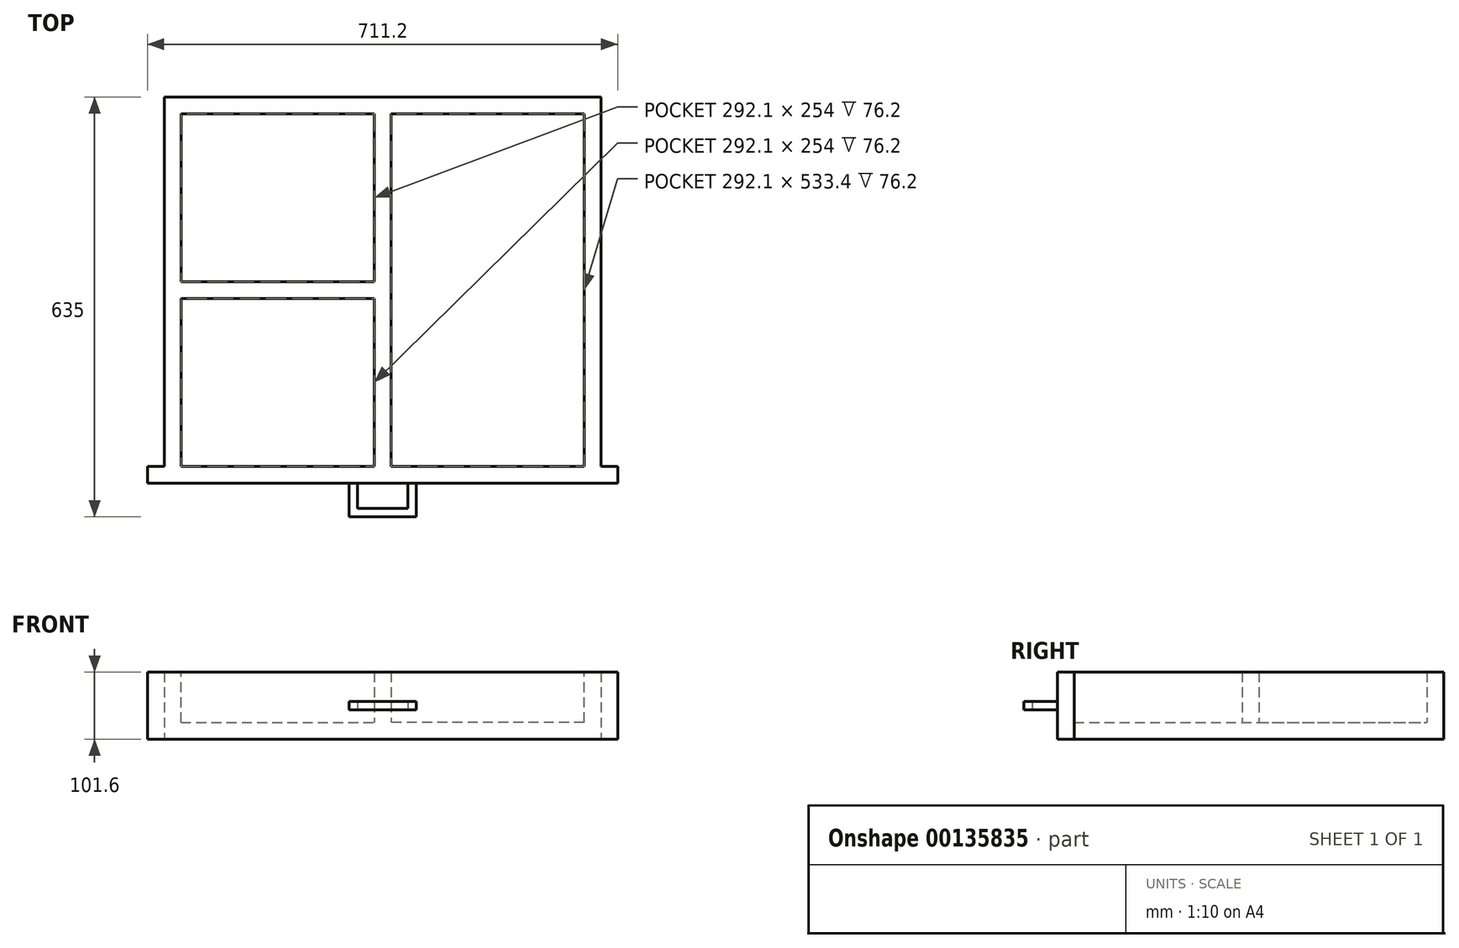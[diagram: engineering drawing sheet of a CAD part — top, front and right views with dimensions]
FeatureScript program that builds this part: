
annotation { "Feature Type Name" : "Feature", "Feature Type Description" : "" }
export const myFeature = defineFeature(function(context is Context, id is Id, definition is map)
    precondition{}
    {
        {
            var Q0;
            Q0=qCreatedBy(makeId("Front.planeOp"),FACE);
            var sketch = newSketch(context, id + "F0", { "sketchPlane" : qUnion([Q0])});
            skLineSegment(sketch, "E0.bottom", {"start": v(-355.6, 50.8) * mm, "end": v(355.6, 50.8) * mm});
            skLineSegment(sketch, "E0.top", {"start": v(-355.6, -50.8) * mm, "end": v(355.6, -50.8) * mm});
            skLineSegment(sketch, "E0.left", {"start": v(-355.6, 50.8) * mm, "end": v(-355.6, -50.8) * mm});
            skLineSegment(sketch, "E0.right", {"start": v(355.6, 50.8) * mm, "end": v(355.6, -50.8) * mm});
            skLineSegment(sketch, "E1", {"start": v(0, -50.8) * mm, "end": v(0, 50.8) * mm, "construction": true});
            skPoint(sketch, "E2", {"position": v(0, 0) * mm});
            skSolve(sketch);
        }
        {
            var Q0;
            Q0=makeQuery(id+"F0.imprint","IMPRINT",FACE,{"disambiguationData":[TD([[makeQuery(id+"F0.imprint","IMPRINT",EDGE,{"derivedFrom":sQuery(id+"F0.wireOp",EDGE,"E0.bottom")}),-1.0]])]});
            extrude(context, id + "F1", {"entities" : qUnion([Q0]), "endBound" : BoundingType.SYMMETRIC, "depth" : 25.4 * mm});
        }
        {
            var Q0;
            Q0=makeQuery(id+"F1.opExtrude","CAP_FACE",FACE,{"disambiguationData":[OSD([sQuery(id+"F0.wireOp",EDGE,"E0.bottom"),sQuery(id+"F0.wireOp",EDGE,"E0.top"),sQuery(id+"F0.wireOp",EDGE,"E0.left"),sQuery(id+"F0.wireOp",EDGE,"E0.right")])],"isStart":true});
            var sketch = newSketch(context, id + "F2", { "sketchPlane" : qUnion([Q0])});
            skLineSegment(sketch, "E3.bottom", {"start": v(-330.2, 50.8) * mm, "end": v(330.2, 50.8) * mm});
            skLineSegment(sketch, "E3.top", {"start": v(-330.2, -50.8) * mm, "end": v(330.2, -50.8) * mm});
            skLineSegment(sketch, "E3.left", {"start": v(-330.2, 50.8) * mm, "end": v(-330.2, -50.8) * mm});
            skLineSegment(sketch, "E3.right", {"start": v(330.2, 50.8) * mm, "end": v(330.2, -50.8) * mm});
            skLineSegment(sketch, "E4", {"start": v(0, 50.8) * mm, "end": v(0, -50.8) * mm, "construction": true});
            skPoint(sketch, "E5", {"position": v(0, 50.8) * mm});
            skSolve(sketch);
        }
        {
            var Q0;
            Q0=makeQuery(id+"F2.imprint","IMPRINT",FACE,{"disambiguationData":[TD([[makeQuery(id+"F2.imprint","IMPRINT",EDGE,{"derivedFrom":sQuery(id+"F2.wireOp",EDGE,"E3.bottom")}),1.0]])]});
            extrude(context, id + "F3", {"entities" : qUnion([Q0]), "operationType" : NewBodyOperationType.ADD, "depth" : 558.8 * mm});
        }
        {
            var Q0;
            Q0=makeQuery(id+"F3.boolean.opBoolean","MERGE",FACE,{"derivedFrom":[makeQuery(id+"F1.opExtrude","SWEPT_FACE",FACE,{"disambiguationData":[OSD([sQuery(id+"F0.wireOp",EDGE,"E0.bottom")])]}),makeQuery(id+"F3.opExtrude","SWEPT_FACE",FACE,{"disambiguationData":[OSD([sQuery(id+"F2.wireOp",EDGE,"E3.bottom")])]})]});
            var sketch = newSketch(context, id + "F4", { "sketchPlane" : qUnion([Q0])});
            skLineSegment(sketch, "E6.bottom", {"start": v(304.8, 12.7) * mm, "end": v(-304.8, 12.7) * mm});
            skLineSegment(sketch, "E6.top", {"start": v(304.8, 546.1) * mm, "end": v(-304.8, 546.1) * mm});
            skLineSegment(sketch, "E6.left", {"start": v(304.8, 12.7) * mm, "end": v(304.8, 546.1) * mm});
            skLineSegment(sketch, "E6.right", {"start": v(-304.8, 12.7) * mm, "end": v(-304.8, 546.1) * mm});
            skSolve(sketch);
        }
        {
            var Q0;
            Q0=makeQuery(id+"F4.imprint","IMPRINT",FACE,{"disambiguationData":[TD([[makeQuery(id+"F4.imprint","IMPRINT",EDGE,{"derivedFrom":sQuery(id+"F4.wireOp",EDGE,"E6.bottom")}),-1.0]])]});
            extrude(context, id + "F5", {"entities" : qUnion([Q0]), "operationType" : NewBodyOperationType.REMOVE, "oppositeDirection" : true, "depth" : 76.2 * mm});
        }
        {
            var Q0;
            Q0=qCreatedBy(makeId("Top.planeOp"),FACE);
            var sketch = newSketch(context, id + "F6", { "sketchPlane" : qUnion([Q0])});
            skLineSegment(sketch, "E7", {"start": v(-50.8, -12.7) * mm, "end": v(50.8, -12.7) * mm, "construction": true});
            skLineSegment(sketch, "E8", {"start": v(-50.8, -12.7) * mm, "end": v(-50.8, -63.5) * mm});
            skLineSegment(sketch, "E9", {"start": v(-50.8, -63.5) * mm, "end": v(50.8, -63.5) * mm});
            skLineSegment(sketch, "E10", {"start": v(50.8, -63.5) * mm, "end": v(50.8, -12.7) * mm});
            skLineSegment(sketch, "E11", {"start": v(0, 0) * mm, "end": v(0, -12.7) * mm, "construction": true});
            skLineSegment(sketch, "E12", {"start": v(-38, -12.7) * mm, "end": v(-38, -50.8) * mm});
            skLineSegment(sketch, "E13", {"start": v(-38, -50.8) * mm, "end": v(38.1, -50.8) * mm});
            skLineSegment(sketch, "E14", {"start": v(38.1, -50.8) * mm, "end": v(38.1, -12.7) * mm});
            skLineSegment(sketch, "E15", {"start": v(38.1, -12.7) * mm, "end": v(50.8, -12.7) * mm});
            skLineSegment(sketch, "E16", {"start": v(-38, -12.7) * mm, "end": v(-50.8, -12.7) * mm});
            skSolve(sketch);
        }
        {
            var Q0;
            Q0=makeQuery(id+"F6.imprint","IMPRINT",FACE,{"disambiguationData":[TD([[makeQuery(id+"F6.imprint","IMPRINT",EDGE,{"derivedFrom":sQuery(id+"F6.wireOp",EDGE,"E8")}),1.0]])]});
            extrude(context, id + "F7", {"entities" : qUnion([Q0]), "operationType" : NewBodyOperationType.ADD, "endBound" : BoundingType.SYMMETRIC, "depth" : 12.7 * mm});
        }
        {
            var Q0;
            Q0=makeQuery(id+"F5.boolean.opBoolean","COPY",FACE,{"derivedFrom":makeQuery(id+"F5.opExtrude","CAP_FACE",FACE,{"disambiguationData":[OSD([sQuery(id+"F4.wireOp",EDGE,"E6.bottom"),sQuery(id+"F4.wireOp",EDGE,"E6.top"),sQuery(id+"F4.wireOp",EDGE,"E6.left"),sQuery(id+"F4.wireOp",EDGE,"E6.right")])],"isStart":false})});
            var sketch = newSketch(context, id + "F8", { "sketchPlane" : qUnion([Q0])});
            skSolve(sketch);
        }
        {
            var Q0;
            Q0=makeQuery(id+"F8.imprint","IMPRINT",FACE,{"disambiguationData":[TD([[makeQuery(id+"F8.imprint","IMPRINT",EDGE,{"derivedFrom":makeQuery(id+"F5.boolean.opBoolean","COPY",EDGE,{"derivedFrom":makeQuery(id+"F5.opExtrude","CAP_EDGE",EDGE,{"disambiguationData":[OSD([sQuery(id+"F4.wireOp",EDGE,"E6.bottom")])],"isStart":false})})}),-1.0]])]});
            var sketch = newSketch(context, id + "F9", { "sketchPlane" : qUnion([Q0])});
            skPoint(sketch, "E17", {"position": v(0, 12.7) * mm});
            skPoint(sketch, "E18", {"position": v(-304.8, 279.4) * mm});
            skLineSegment(sketch, "E19.bottom", {"start": v(-304.8, 292.1) * mm, "end": v(-12.7, 292.1) * mm});
            skLineSegment(sketch, "E19.top", {"start": v(-304.8, 266.7) * mm, "end": v(-12.7, 266.7) * mm});
            skLineSegment(sketch, "E19.left", {"start": v(-304.8, 292.1) * mm, "end": v(-304.8, 266.7) * mm});
            skLineSegment(sketch, "E19.right", {"start": v(-12.7, 292.1) * mm, "end": v(-12.7, 266.7) * mm});
            skLineSegment(sketch, "E20.bottom", {"start": v(-12.7, 12.7) * mm, "end": v(12.7, 12.7) * mm});
            skLineSegment(sketch, "E20.top", {"start": v(-12.7, 546.1) * mm, "end": v(12.7, 546.1) * mm});
            skLineSegment(sketch, "E20.left", {"start": v(-12.7, 12.7) * mm, "end": v(-12.7, 546.1) * mm});
            skLineSegment(sketch, "E20.right", {"start": v(12.7, 12.7) * mm, "end": v(12.7, 546.1) * mm});
            skSolve(sketch);
        }
        {
            var Q0;
            Q0 = qSketchRegion(id + "F9", true);
            extrude(context, id + "F10", {"entities" : qUnion([Q0]), "operationType" : NewBodyOperationType.ADD, "depth" : 76.2 * mm});
        }
    });
